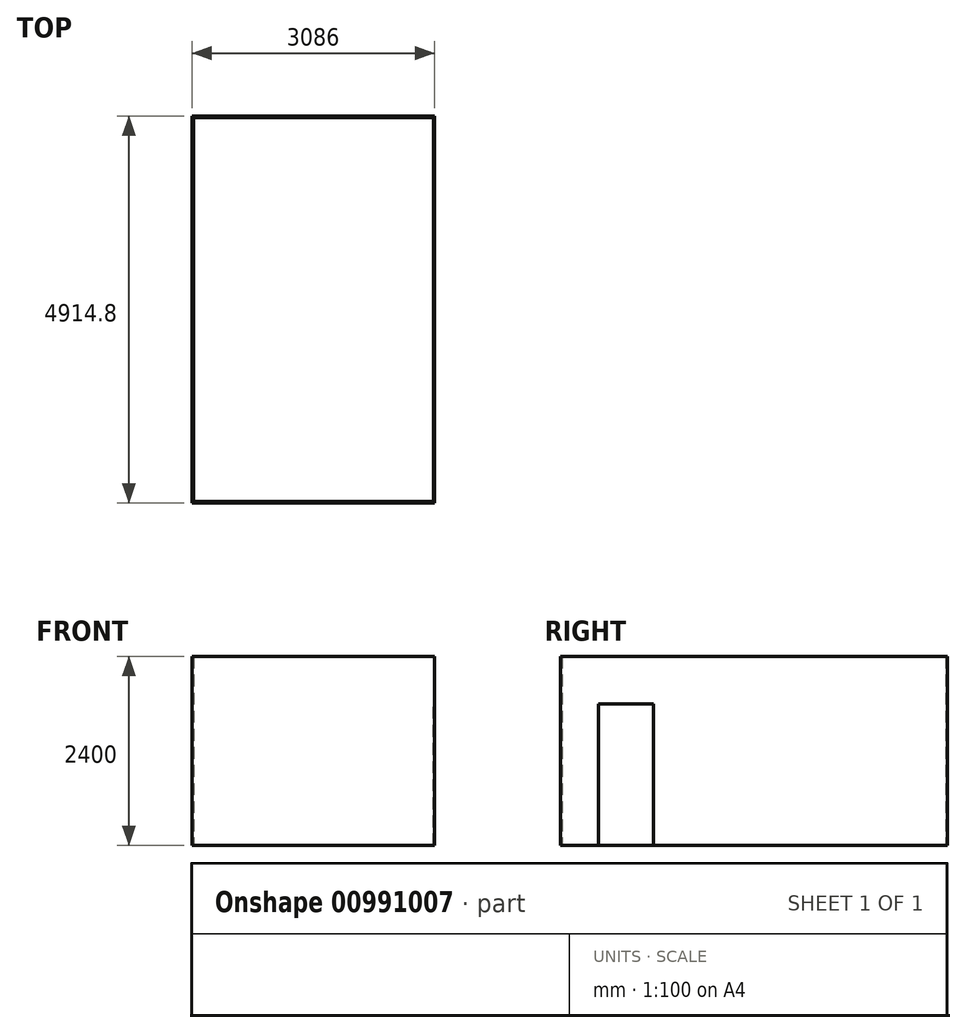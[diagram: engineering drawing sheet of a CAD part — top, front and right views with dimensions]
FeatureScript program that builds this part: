
annotation { "Feature Type Name" : "Feature", "Feature Type Description" : "" }
export const myFeature = defineFeature(function(context is Context, id is Id, definition is map)
    precondition{}
    {
        {
            var Q0;
            Q0=qCreatedBy(makeId("Top.planeOp"),FACE);
            var sketch = newSketch(context, id + "F0", { "sketchPlane" : qUnion([Q0])});
            skLineSegment(sketch, "E0.bottom", {"start": v(1524, -2438.4) * mm, "end": v(-1524, -2438.4) * mm});
            skLineSegment(sketch, "E0.top", {"start": v(1524, 2438.4) * mm, "end": v(-1524, 2438.4) * mm});
            skLineSegment(sketch, "E0.left", {"start": v(1524, -2438.4) * mm, "end": v(1524, 2438.4) * mm});
            skLineSegment(sketch, "E0.right", {"start": v(-1524, -2438.4) * mm, "end": v(-1524, 2438.4) * mm});
            skPoint(sketch, "E0.middle", {"position": v(0, 0) * mm});
            skLineSegment(sketch, "E1.0", {"start": v(1543, -2457.4) * mm, "end": v(1543, 2457.4) * mm});
            skLineSegment(sketch, "E1.1", {"start": v(1543, -2457.4) * mm, "end": v(-1543, -2457.4) * mm});
            skLineSegment(sketch, "E1.2", {"start": v(-1543, -2457.4) * mm, "end": v(-1543, 2457.4) * mm});
            skLineSegment(sketch, "E1.3", {"start": v(1543, 2457.4) * mm, "end": v(-1543, 2457.4) * mm});
            skSolve(sketch);
        }
        {
            var Q0;
            Q0 = qSketchRegion(id + "F0", true);
            extrude(context, id + "F1", {"entities" : qUnion([Q0]), "depth" : 2400 * mm, "offsetDistance" : 25 * mm});
        }
        {
            var Q0;
            Q0=makeQuery(id+"F1.opExtrude","SWEPT_FACE",FACE,{"disambiguationData":[OSD([sQuery(id+"F0.wireOp",EDGE,"E1.0")])]});
            var sketch = newSketch(context, id + "F2", { "sketchPlane" : qUnion([Q0])});
            skLineSegment(sketch, "E2.bottom", {"start": v(-1980.12, 0) * mm, "end": v(-1280.12, 0) * mm});
            skLineSegment(sketch, "E2.top", {"start": v(-1980.12, 1800) * mm, "end": v(-1280.12, 1800) * mm});
            skLineSegment(sketch, "E2.left", {"start": v(-1980.12, 0) * mm, "end": v(-1980.12, 1800) * mm});
            skLineSegment(sketch, "E2.right", {"start": v(-1280.12, 0) * mm, "end": v(-1280.12, 1800) * mm});
            skSolve(sketch);
        }
        {
            var Q0;
            Q0 = qSketchRegion(id + "F2", true);
            extrude(context, id + "F3", {"entities" : qUnion([Q0]), "operationType" : NewBodyOperationType.REMOVE, "endBound" : BoundingType.UP_TO_NEXT, "oppositeDirection" : true, "depth" : 25 * mm, "offsetDistance" : 25 * mm});
        }
    });
